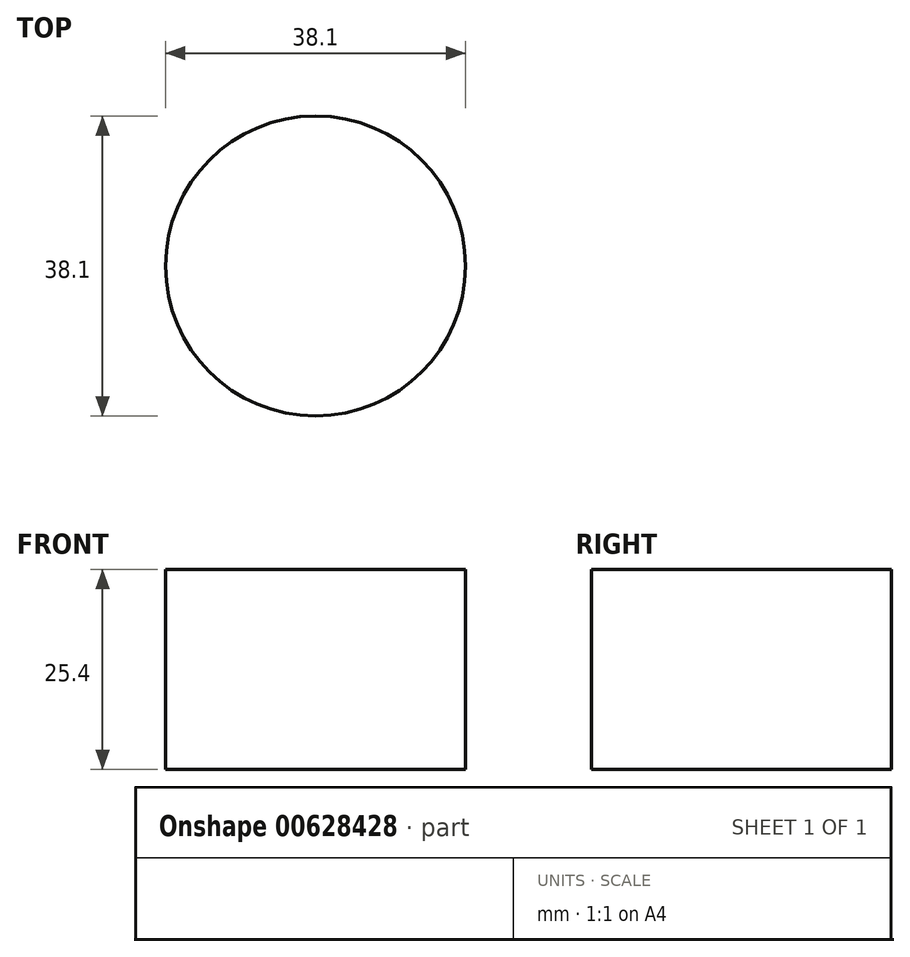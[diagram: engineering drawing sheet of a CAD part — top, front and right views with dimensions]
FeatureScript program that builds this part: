
annotation { "Feature Type Name" : "Feature", "Feature Type Description" : "" }
export const myFeature = defineFeature(function(context is Context, id is Id, definition is map)
    precondition{}
    {
        {
            var Q0;
            Q0=qCreatedBy(makeId("Top.planeOp"),FACE);
            var sketch = newSketch(context, id + "F0", { "sketchPlane" : qUnion([Q0])});
            skCircle(sketch, "E0", {"center": v(0, 0) * mm, "radius": 19.05 * mm});
            skSolve(sketch);
        }
        {
            var Q0;
            Q0=makeQuery(id+"F0.imprint","IMPRINT",FACE,{"disambiguationData":[TD([[makeQuery(id+"F0.imprint","IMPRINT",EDGE,{"derivedFrom":sQuery(id+"F0.wireOp",EDGE,"E0")}),1.0]])]});
            extrude(context, id + "F1", {"entities" : qUnion([Q0]), "depth" : 25.4 * mm, "offsetDistance" : 25.4 * mm});
        }
    });
